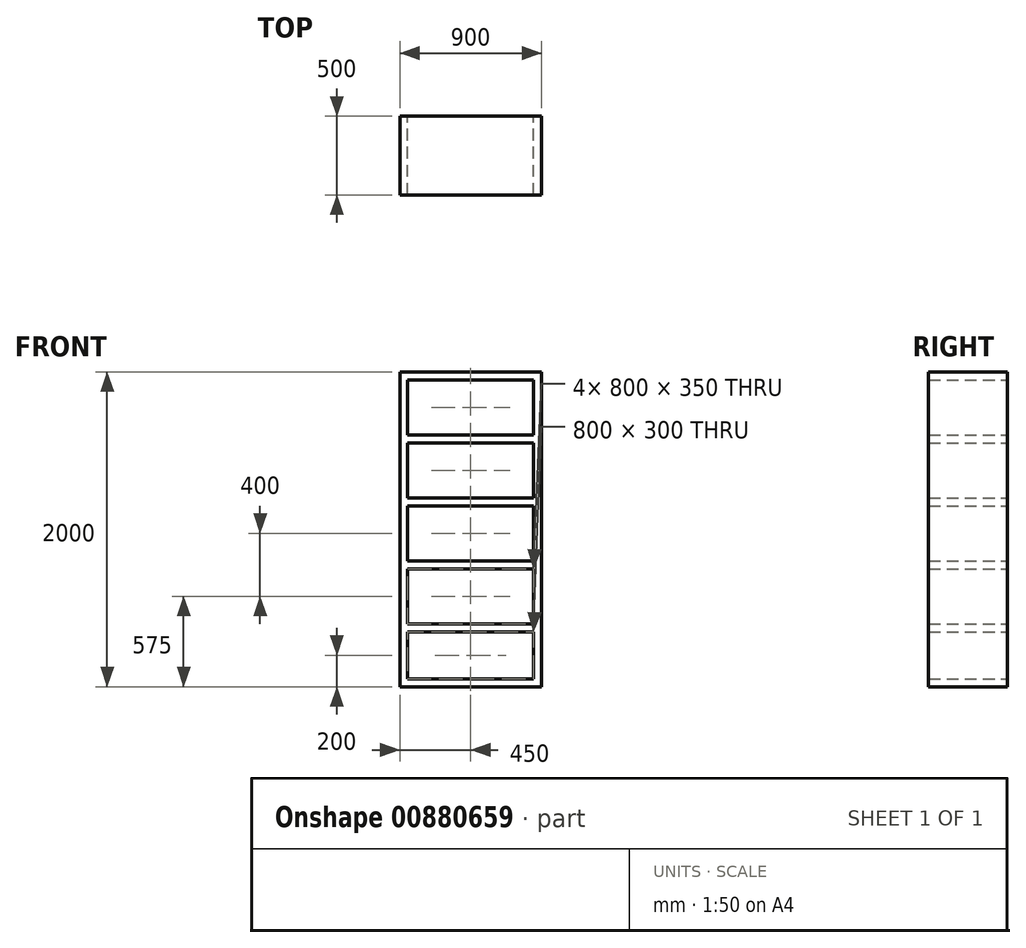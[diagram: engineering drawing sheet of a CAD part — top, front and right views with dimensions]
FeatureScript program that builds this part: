
annotation { "Feature Type Name" : "Feature", "Feature Type Description" : "" }
export const myFeature = defineFeature(function(context is Context, id is Id, definition is map)
    precondition{}
    {
        {
            var Q0;
            Q0=qCreatedBy(makeId("Front.planeOp"),FACE);
            var sketch = newSketch(context, id + "F0", { "sketchPlane" : qUnion([Q0])});
            skLineSegment(sketch, "E0.bottom", {"start": v(450, 1000) * mm, "end": v(-450, 1000) * mm});
            skLineSegment(sketch, "E0.top", {"start": v(450, -1000) * mm, "end": v(-450, -1000) * mm});
            skLineSegment(sketch, "E0.left", {"start": v(450, 1000) * mm, "end": v(450, -1000) * mm});
            skLineSegment(sketch, "E0.right", {"start": v(-450, 1000) * mm, "end": v(-450, -1000) * mm});
            skPoint(sketch, "E0.middle", {"position": v(0, 0) * mm});
            skLineSegment(sketch, "E1.bottom", {"start": v(400, 950) * mm, "end": v(-400, 950) * mm});
            skLineSegment(sketch, "E1.top", {"start": v(400, -950) * mm, "end": v(-400, -950) * mm});
            skLineSegment(sketch, "E1.left", {"start": v(400, 950) * mm, "end": v(400, 600) * mm});
            skLineSegment(sketch, "E1.right", {"start": v(-400, 950) * mm, "end": v(-400, 600) * mm});
            skLineSegment(sketch, "E2.bottom", {"start": v(-400, 600) * mm, "end": v(400, 600) * mm});
            skLineSegment(sketch, "E2.top", {"start": v(-400, 550) * mm, "end": v(400, 550) * mm});
            skLineSegment(sketch, "E3.trimOffspring", {"start": v(-400, 550) * mm, "end": v(-400, 200) * mm});
            skLineSegment(sketch, "E4.trimOffspring", {"start": v(400, 550) * mm, "end": v(400, 200) * mm});
            skLineSegment(sketch, "E5.0.1.0", {"start": v(-400, 200) * mm, "end": v(400, 200) * mm});
            skLineSegment(sketch, "E5.0.1.1", {"start": v(-400, 150) * mm, "end": v(400, 150) * mm});
            skLineSegment(sketch, "E5.0.2.0", {"start": v(-400, -200) * mm, "end": v(400, -200) * mm});
            skLineSegment(sketch, "E5.0.2.1", {"start": v(-400, -250) * mm, "end": v(400, -250) * mm});
            skLineSegment(sketch, "E5.0.3.0", {"start": v(-400, -600) * mm, "end": v(400, -600) * mm});
            skLineSegment(sketch, "E5.0.3.1", {"start": v(-400, -650) * mm, "end": v(400, -650) * mm});
            skLineSegment(sketch, "E5.direction1", {"start": v(-400, 600) * mm, "end": v(-50, 600) * mm, "construction": true});
            skLineSegment(sketch, "E5.direction2", {"start": v(-400, 600) * mm, "end": v(-400, 200) * mm, "construction": true});
            skLineSegment(sketch, "E6.trimOffspring", {"start": v(-400, 150) * mm, "end": v(-400, -200) * mm});
            skLineSegment(sketch, "E7.trimOffspring", {"start": v(400, 150) * mm, "end": v(400, -200) * mm});
            skLineSegment(sketch, "E8.trimOffspring", {"start": v(-400, -250) * mm, "end": v(-400, -600) * mm});
            skLineSegment(sketch, "E9.trimOffspring", {"start": v(400, -250) * mm, "end": v(400, -600) * mm});
            skLineSegment(sketch, "E10.trimOffspring", {"start": v(-400, -650) * mm, "end": v(-400, -950) * mm});
            skLineSegment(sketch, "E11.trimOffspring", {"start": v(400, -650) * mm, "end": v(400, -950) * mm});
            skSolve(sketch);
        }
        {
            var Q0;
            Q0=makeQuery(id+"F0.imprint","IMPRINT",FACE,{"disambiguationData":[TD([[makeQuery(id+"F0.imprint","IMPRINT",EDGE,{"derivedFrom":sQuery(id+"F0.wireOp",EDGE,"E0.bottom")}),1.0]])]});
            extrude(context, id + "F1", {"entities" : qUnion([Q0]), "depth" : 500 * mm, "offsetDistance" : 25 * mm});
        }
    });
